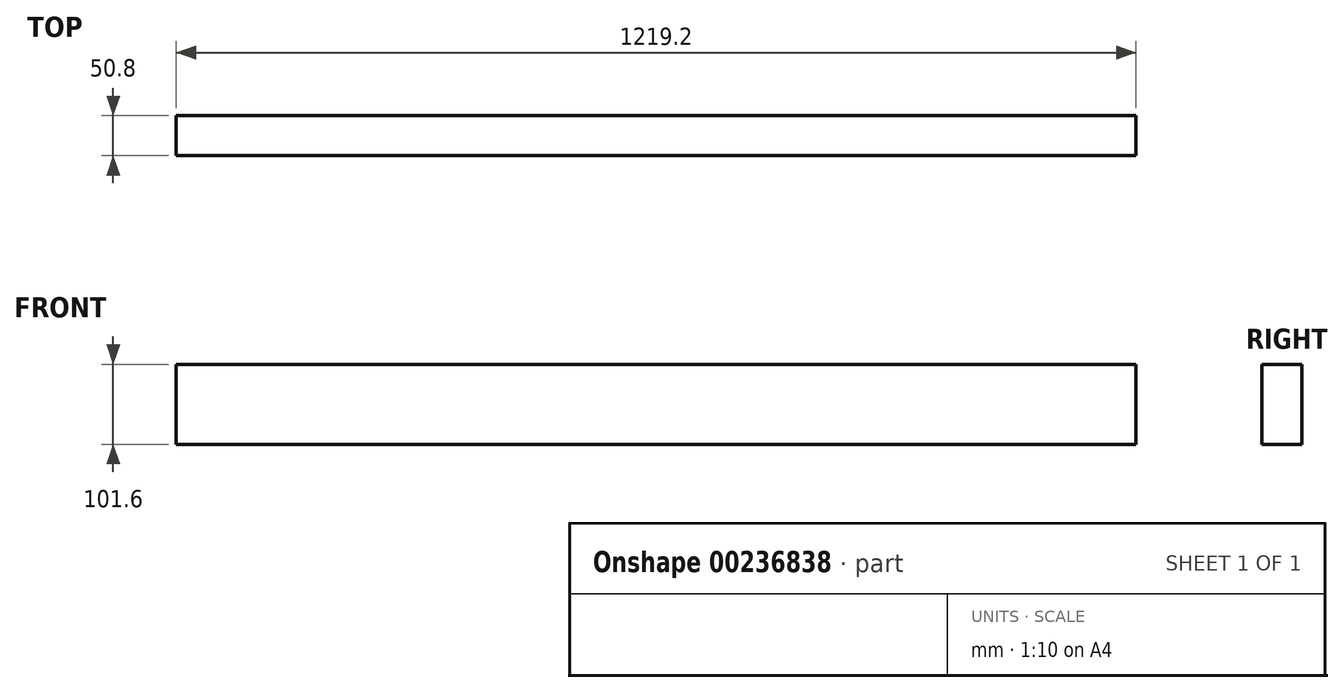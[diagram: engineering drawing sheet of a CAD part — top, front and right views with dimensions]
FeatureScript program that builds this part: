
annotation { "Feature Type Name" : "Feature", "Feature Type Description" : "" }
export const myFeature = defineFeature(function(context is Context, id is Id, definition is map)
    precondition{}
    {
        {
            var Q0;
            Q0=qCreatedBy(makeId("Top.planeOp"),FACE);
            var sketch = newSketch(context, id + "F0", { "sketchPlane" : qUnion([Q0])});
            skLineSegment(sketch, "E0.bottom", {"start": v(609.6, 25.4) * mm, "end": v(-609.6, 25.4) * mm});
            skLineSegment(sketch, "E0.top", {"start": v(609.6, -25.4) * mm, "end": v(-609.6, -25.4) * mm});
            skLineSegment(sketch, "E0.left", {"start": v(609.6, 25.4) * mm, "end": v(609.6, -25.4) * mm});
            skLineSegment(sketch, "E0.right", {"start": v(-609.6, 25.4) * mm, "end": v(-609.6, -25.4) * mm});
            skPoint(sketch, "E0.middle", {"position": v(0, 0) * mm});
            skSolve(sketch);
        }
        {
            var Q0;
            Q0=qSketchRegion(id+"F0",true);
            extrude(context, id + "F1", {"entities" : qUnion([Q0]), "endBound" : BoundingType.SYMMETRIC, "depth" : 101.6 * mm});
        }
    });
